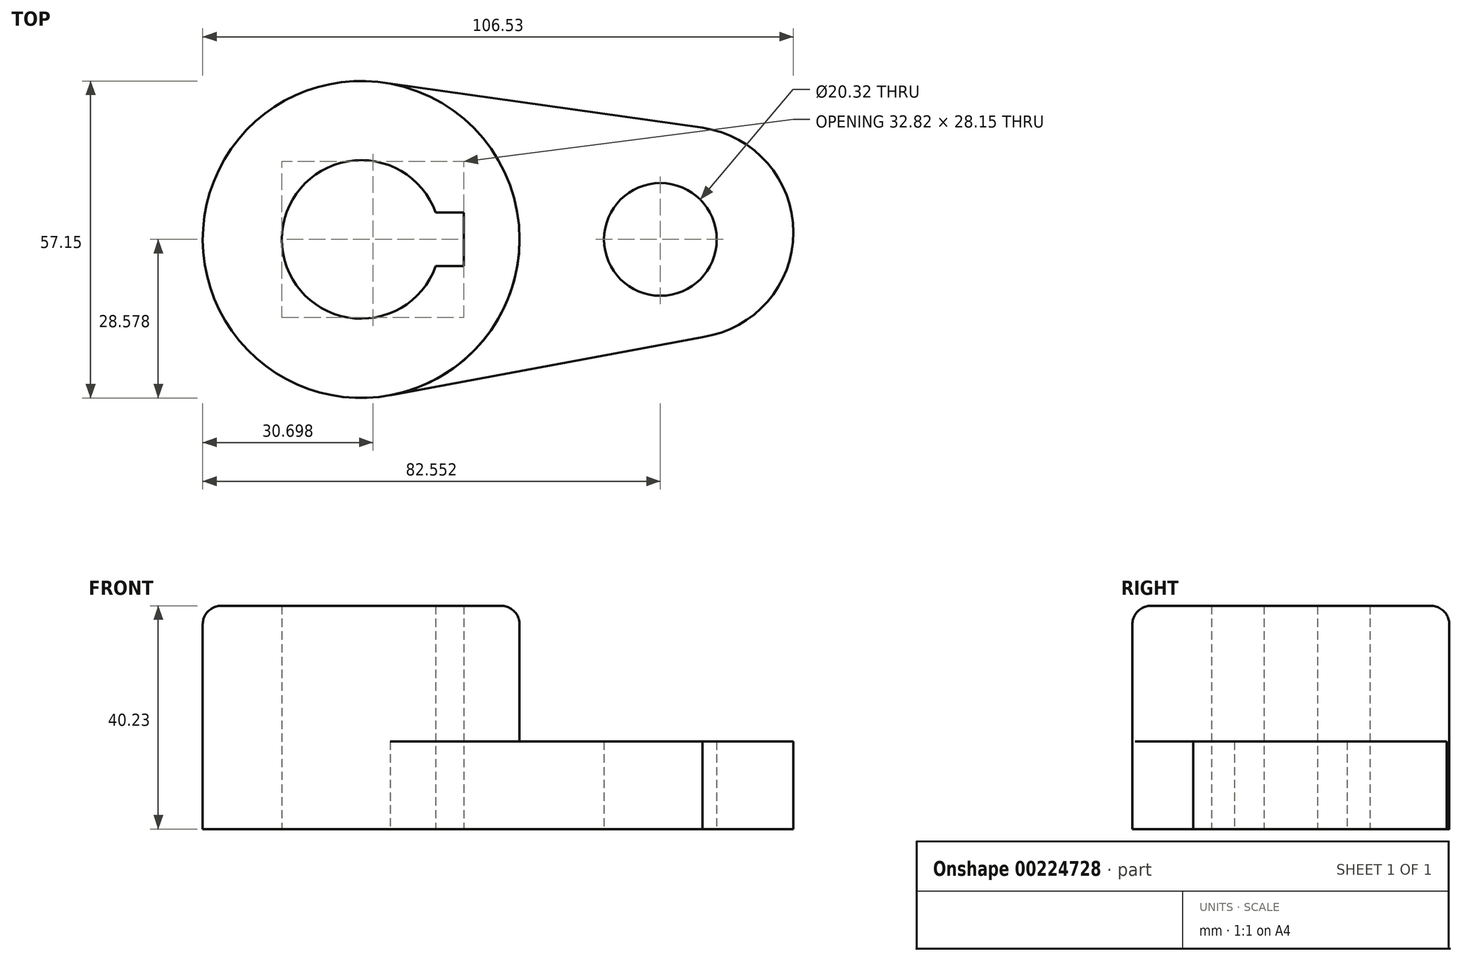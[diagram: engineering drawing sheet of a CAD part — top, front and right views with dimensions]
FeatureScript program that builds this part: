
annotation { "Feature Type Name" : "Feature", "Feature Type Description" : "" }
export const myFeature = defineFeature(function(context is Context, id is Id, definition is map)
    precondition{}
    {
        {
            var Q0;
            Q0=qCreatedBy(makeId("Top.planeOp"),FACE);
            var sketch = newSketch(context, id + "F0", { "sketchPlane" : qUnion([Q0])});
            skCircle(sketch, "E0", {"center": v(-48.06, 12.4) * mm, "radius": 28.58 * mm});
            skCircle(sketch, "E1", {"center": v(5.91, 12.4) * mm, "radius": 10.16 * mm});
            skArc(sketch, "E2", {"start": v(-34.62, 17.23) * mm, "mid": v(-62.35, 12.4) * mm, "end": v(-34.62, 7.58) * mm});
            skLineSegment(sketch, "E3.bottom", {"start": v(-34.62, 17.23) * mm, "end": v(-29.53, 17.23) * mm});
            skLineSegment(sketch, "E3.top", {"start": v(-34.62, 7.58) * mm, "end": v(-29.53, 7.58) * mm});
            skLineSegment(sketch, "E3.right", {"start": v(-29.53, 17.23) * mm, "end": v(-29.53, 7.58) * mm});
            skPoint(sketch, "E3.middle", {"position": v(-32.07, 12.4) * mm});
            skLineSegment(sketch, "E4", {"start": v(-42.83, 40.5) * mm, "end": v(13.5, 32.54) * mm});
            skLineSegment(sketch, "E5", {"start": v(-42.83, -15.68) * mm, "end": v(13.5, -5.18) * mm});
            skArc(sketch, "E6", {"start": v(13.5, 32.54) * mm, "mid": v(29.9, 13.68) * mm, "end": v(13.5, -5.18) * mm});
            skSolve(sketch);
        }
        {
            var Q0;
            Q0=makeQuery(id+"F0.imprint","IMPRINT",FACE,{"disambiguationData":[TD([[makeQuery(id+"F0.imprint","IMPRINT",EDGE,{"derivedFrom":sQuery(id+"F0.wireOp",EDGE,"E2")}),-1.0]])]});
            extrude(context, id + "F1", {"entities" : qUnion([Q0]), "depth" : 40.23 * mm});
        }
        {
            var Q0;
            Q0 = qSketchRegion(id + "F0", true);
            extrude(context, id + "F2", {"entities" : qUnion([Q0]), "operationType" : NewBodyOperationType.ADD, "depth" : 15.77 * mm});
        }
        {
            var Q0;
            Q0=makeQuery(id+"F1.opExtrude","CAP_EDGE",EDGE,{"disambiguationData":[OSD([sQuery(id+"F0.wireOp",EDGE,"E0")])],"isStart":false});
            fillet(context, id + "F3", {"entities" : qUnion([Q0]), "radius" : 3.3 * mm, "tangentPropagation" : true, "allowEdgeOverflow" : false});
        }
    });
